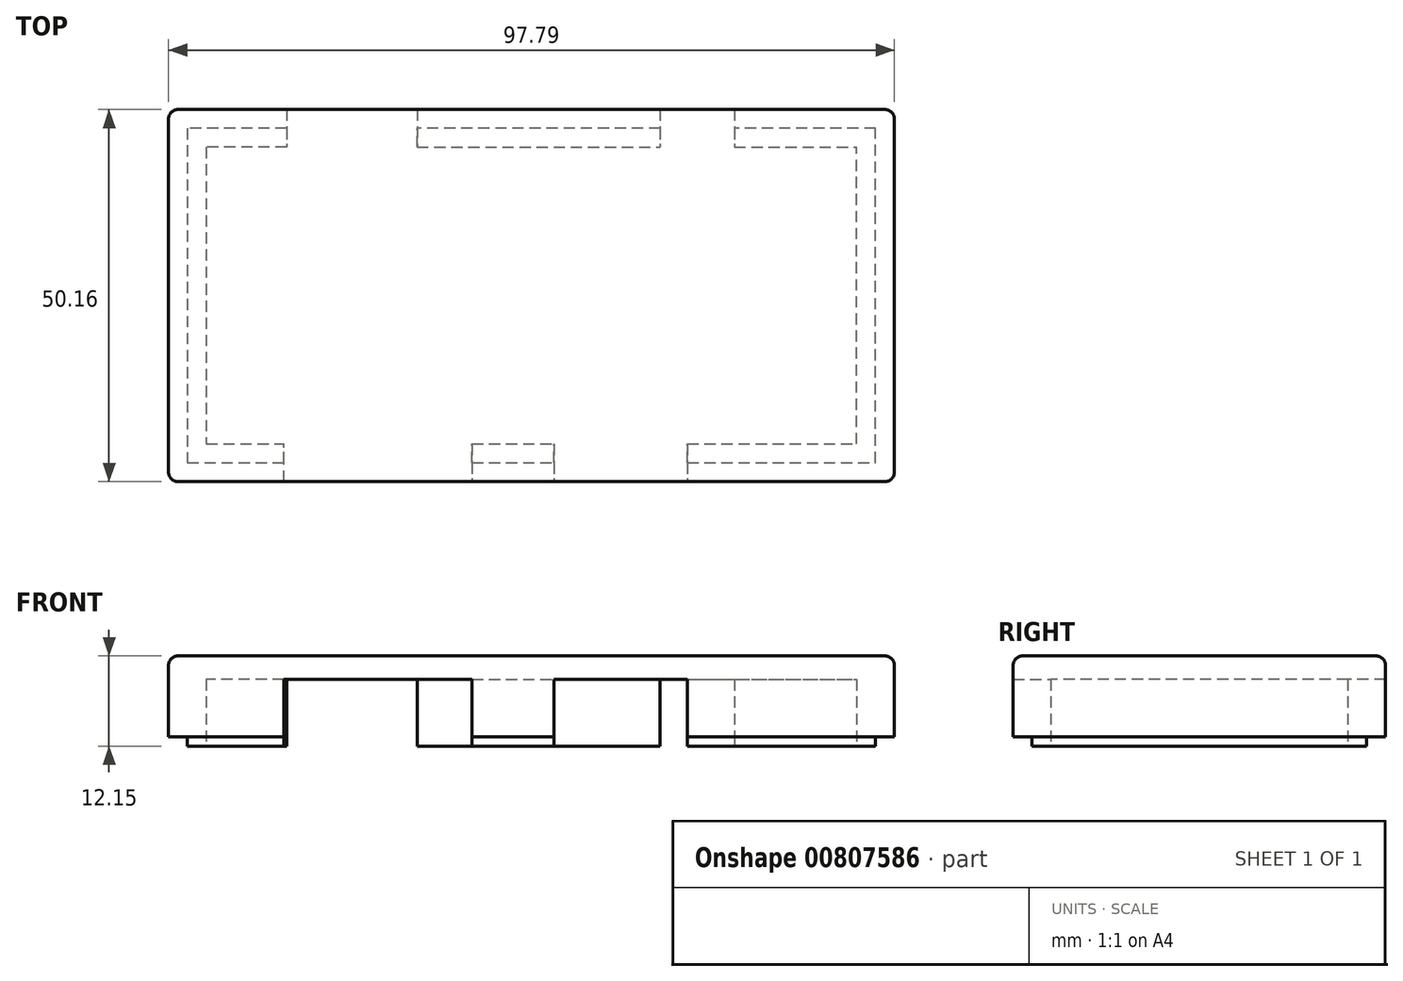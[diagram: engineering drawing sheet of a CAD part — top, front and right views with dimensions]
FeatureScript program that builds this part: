
annotation { "Feature Type Name" : "Feature", "Feature Type Description" : "" }
export const myFeature = defineFeature(function(context is Context, id is Id, definition is map)
    precondition{}
    {
        {
            var Q0;
            Q0=qCreatedBy(makeId("Top.planeOp"),FACE);
            var sketch = newSketch(context, id + "F0", { "sketchPlane" : qUnion([Q0])});
            skLineSegment(sketch, "E0.0", {"start": v(13.35, 45.09) * mm, "end": v(0, 45.09) * mm});
            skLineSegment(sketch, "E0.1", {"start": v(0, 45.09) * mm, "end": v(0, 0) * mm});
            skLineSegment(sketch, "E0.2", {"start": v(0, 0) * mm, "end": v(12.99, 0) * mm});
            skLineSegment(sketch, "E0.3", {"start": v(2.54, 2.54) * mm, "end": v(12.99, 2.54) * mm});
            skLineSegment(sketch, "E0.4", {"start": v(2.54, 42.55) * mm, "end": v(2.54, 2.54) * mm});
            skLineSegment(sketch, "E0.5", {"start": v(90.17, 42.55) * mm, "end": v(73.69, 42.55) * mm});
            skLineSegment(sketch, "E0.6", {"start": v(13.35, 45.09) * mm, "end": v(13.35, 47.63) * mm, "construction": true});
            skLineSegment(sketch, "E0.7", {"start": v(30.95, 45.09) * mm, "end": v(30.95, 47.63) * mm, "construction": true});
            skLineSegment(sketch, "E0.8", {"start": v(63.69, 45.09) * mm, "end": v(30.95, 45.09) * mm});
            skLineSegment(sketch, "E0.9", {"start": v(63.69, 45.09) * mm, "end": v(63.69, 47.63) * mm, "construction": true});
            skLineSegment(sketch, "E0.10", {"start": v(73.69, 45.09) * mm, "end": v(73.69, 47.63) * mm, "construction": true});
            skLineSegment(sketch, "E0.11", {"start": v(92.71, 45.09) * mm, "end": v(73.69, 45.09) * mm});
            skLineSegment(sketch, "E0.12", {"start": v(90.17, 2.54) * mm, "end": v(90.17, 42.55) * mm});
            skLineSegment(sketch, "E0.13", {"start": v(92.71, 0) * mm, "end": v(92.71, 45.09) * mm});
            skLineSegment(sketch, "E0.14", {"start": v(67.35, 0) * mm, "end": v(92.71, 0) * mm});
            skLineSegment(sketch, "E0.15", {"start": v(67.35, 0) * mm, "end": v(67.35, -2.54) * mm, "construction": true});
            skLineSegment(sketch, "E0.16", {"start": v(49.35, 0) * mm, "end": v(49.35, -2.54) * mm, "construction": true});
            skLineSegment(sketch, "E0.17", {"start": v(38.34, 0) * mm, "end": v(49.35, 0) * mm});
            skLineSegment(sketch, "E0.18", {"start": v(38.34, 0) * mm, "end": v(38.34, -2.54) * mm, "construction": true});
            skLineSegment(sketch, "E0.19", {"start": v(12.99, 0) * mm, "end": v(12.99, -2.54) * mm, "construction": true});
            skLineSegment(sketch, "E1", {"start": v(13.35, 45.09) * mm, "end": v(13.35, 42.55) * mm});
            skLineSegment(sketch, "E2", {"start": v(30.95, 42.55) * mm, "end": v(30.95, 45.09) * mm});
            skLineSegment(sketch, "E3", {"start": v(63.69, 45.09) * mm, "end": v(63.69, 42.55) * mm});
            skLineSegment(sketch, "E4", {"start": v(73.69, 45.09) * mm, "end": v(73.69, 42.55) * mm});
            skLineSegment(sketch, "E5.trimOffspring", {"start": v(13.35, 42.55) * mm, "end": v(2.54, 42.55) * mm});
            skLineSegment(sketch, "E6.trimOffspring", {"start": v(63.69, 42.55) * mm, "end": v(30.95, 42.55) * mm});
            skLineSegment(sketch, "E7", {"start": v(12.99, 0) * mm, "end": v(12.99, 2.54) * mm});
            skLineSegment(sketch, "E8", {"start": v(38.34, 0) * mm, "end": v(38.34, 2.54) * mm});
            skLineSegment(sketch, "E9", {"start": v(49.35, 0) * mm, "end": v(49.35, 2.54) * mm});
            skLineSegment(sketch, "E10", {"start": v(67.35, 0) * mm, "end": v(67.35, 2.54) * mm});
            skLineSegment(sketch, "E11.trimOffspring", {"start": v(38.34, 2.54) * mm, "end": v(49.35, 2.54) * mm});
            skLineSegment(sketch, "E12.trimOffspring", {"start": v(67.35, 2.54) * mm, "end": v(90.17, 2.54) * mm});
            skSolve(sketch);
        }
        {
            var Q0;
            Q0 = qSketchRegion(id + "F0", true);
            extrude(context, id + "F1", {"entities" : qUnion([Q0]), "depth" : 1.27 * mm, "offsetDistance" : 25.4 * mm});
        }
        {
            var Q0;
            Q0=makeQuery(id+"F1.opExtrude","CAP_FACE",FACE,{"disambiguationData":[OSD([sQuery(id+"F0.wireOp",EDGE,"E0.0"),sQuery(id+"F0.wireOp",EDGE,"E0.1"),sQuery(id+"F0.wireOp",EDGE,"E0.2"),sQuery(id+"F0.wireOp",EDGE,"E0.3"),sQuery(id+"F0.wireOp",EDGE,"E0.4"),sQuery(id+"F0.wireOp",EDGE,"E1"),sQuery(id+"F0.wireOp",EDGE,"E5.trimOffspring"),sQuery(id+"F0.wireOp",EDGE,"E7")])],"isStart":false});
            var sketch = newSketch(context, id + "F2", { "sketchPlane" : qUnion([Q0])});
            skPoint(sketch, "E13.0", {"position": v(2.54, 2.54) * mm});
            skPoint(sketch, "E13.1", {"position": v(90.17, 42.55) * mm});
            skLineSegment(sketch, "E14.bottom", {"start": v(2.54, 2.54) * mm, "end": v(12.99, 2.54) * mm});
            skLineSegment(sketch, "E14.top", {"start": v(2.54, 42.55) * mm, "end": v(13.35, 42.55) * mm});
            skLineSegment(sketch, "E14.left", {"start": v(2.54, 2.54) * mm, "end": v(2.54, 42.55) * mm});
            skLineSegment(sketch, "E14.right", {"start": v(90.17, 2.54) * mm, "end": v(90.17, 42.55) * mm});
            skLineSegment(sketch, "E15.0", {"start": v(-2.54, 47.63) * mm, "end": v(13.35, 47.63) * mm});
            skLineSegment(sketch, "E15.1", {"start": v(-2.54, -2.54) * mm, "end": v(-2.54, 47.63) * mm});
            skLineSegment(sketch, "E15.2", {"start": v(-2.54, -2.54) * mm, "end": v(12.99, -2.54) * mm});
            skLineSegment(sketch, "E15.3", {"start": v(95.25, -2.54) * mm, "end": v(95.25, 47.63) * mm});
            skLineSegment(sketch, "E16", {"start": v(13.35, 42.55) * mm, "end": v(13.35, 47.63) * mm});
            skLineSegment(sketch, "E17", {"start": v(30.95, 47.63) * mm, "end": v(30.95, 42.55) * mm});
            skLineSegment(sketch, "E18", {"start": v(63.69, 47.63) * mm, "end": v(63.69, 42.55) * mm});
            skLineSegment(sketch, "E19", {"start": v(73.69, 47.63) * mm, "end": v(73.69, 42.55) * mm});
            skLineSegment(sketch, "E20", {"start": v(12.99, 2.54) * mm, "end": v(12.99, -2.54) * mm});
            skLineSegment(sketch, "E21", {"start": v(38.34, 2.54) * mm, "end": v(38.34, -2.54) * mm});
            skLineSegment(sketch, "E22", {"start": v(49.35, 2.54) * mm, "end": v(49.35, -2.54) * mm});
            skLineSegment(sketch, "E23", {"start": v(67.35, 2.54) * mm, "end": v(67.35, -2.54) * mm});
            skLineSegment(sketch, "E24.trimOffspring", {"start": v(30.95, 42.55) * mm, "end": v(63.69, 42.55) * mm});
            skLineSegment(sketch, "E25.trimOffspring", {"start": v(30.95, 47.63) * mm, "end": v(63.69, 47.63) * mm});
            skLineSegment(sketch, "E26.trimOffspring", {"start": v(73.69, 47.63) * mm, "end": v(95.25, 47.63) * mm});
            skLineSegment(sketch, "E27.trimOffspring", {"start": v(73.69, 42.55) * mm, "end": v(90.17, 42.55) * mm});
            skLineSegment(sketch, "E28.trimOffspring", {"start": v(67.35, -2.54) * mm, "end": v(95.25, -2.54) * mm});
            skLineSegment(sketch, "E29.trimOffspring", {"start": v(67.35, 2.54) * mm, "end": v(90.17, 2.54) * mm});
            skLineSegment(sketch, "E30.trimOffspring", {"start": v(38.34, 2.54) * mm, "end": v(49.35, 2.54) * mm});
            skLineSegment(sketch, "E31.trimOffspring", {"start": v(38.34, -2.54) * mm, "end": v(49.35, -2.54) * mm});
            skSolve(sketch);
        }
        {
            var Q0;
            Q0 = qSketchRegion(id + "F2", true);
            extrude(context, id + "F3", {"entities" : qUnion([Q0]), "operationType" : NewBodyOperationType.ADD, "depth" : 7.7 * mm, "offsetDistance" : 25.4 * mm});
        }
        {
            var Q0;
            Q0=makeQuery(id+"F3.opExtrude","CAP_FACE",FACE,{"disambiguationData":[OSD([sQuery(id+"F2.wireOp",EDGE,"E14.bottom"),sQuery(id+"F2.wireOp",EDGE,"E14.top"),sQuery(id+"F2.wireOp",EDGE,"E14.left"),sQuery(id+"F2.wireOp",EDGE,"E15.0"),sQuery(id+"F2.wireOp",EDGE,"E15.1"),sQuery(id+"F2.wireOp",EDGE,"E15.2"),sQuery(id+"F2.wireOp",EDGE,"E16"),sQuery(id+"F2.wireOp",EDGE,"E20")])],"isStart":false});
            var sketch = newSketch(context, id + "F4", { "sketchPlane" : qUnion([Q0])});
            skPoint(sketch, "E32.0", {"position": v(95.25, 47.63) * mm});
            skPoint(sketch, "E33.0", {"position": v(-2.54, -2.54) * mm});
            skLineSegment(sketch, "E34.bottom", {"start": v(-2.54, -2.54) * mm, "end": v(95.25, -2.54) * mm});
            skLineSegment(sketch, "E34.top", {"start": v(-2.54, 47.63) * mm, "end": v(95.25, 47.63) * mm});
            skLineSegment(sketch, "E34.left", {"start": v(-2.54, -2.54) * mm, "end": v(-2.54, 47.63) * mm});
            skLineSegment(sketch, "E34.right", {"start": v(95.25, -2.54) * mm, "end": v(95.25, 47.63) * mm});
            skSolve(sketch);
        }
        {
            var Q0;
            Q0 = qSketchRegion(id + "F4", true);
            extrude(context, id + "F5", {"entities" : qUnion([Q0]), "operationType" : NewBodyOperationType.ADD, "depth" : 3.17 * mm, "offsetDistance" : 25.4 * mm});
        }
        {
            var Q0;
            Q0=makeQuery(id+"F5.boolean.opBoolean","MERGE",EDGE,{"derivedFrom":[makeQuery(id+"F3.opExtrude","SWEPT_EDGE",EDGE,{"disambiguationData":[OSD([sQuery(id+"F2.wireOp",EDGE,"E15.3"),sQuery(id+"F2.wireOp",EDGE,"E28.trimOffspring")])]}),makeQuery(id+"F5.opExtrude","SWEPT_EDGE",EDGE,{"disambiguationData":[OSD([sQuery(id+"F4.wireOp",EDGE,"E34.bottom"),sQuery(id+"F4.wireOp",EDGE,"E34.right")])]})]});
            var Q1;
            Q1=makeQuery(id+"F5.boolean.opBoolean","MERGE",EDGE,{"derivedFrom":[makeQuery(id+"F3.opExtrude","SWEPT_EDGE",EDGE,{"disambiguationData":[OSD([sQuery(id+"F2.wireOp",EDGE,"E15.1"),sQuery(id+"F2.wireOp",EDGE,"E15.2")])]}),makeQuery(id+"F5.opExtrude","SWEPT_EDGE",EDGE,{"disambiguationData":[OSD([sQuery(id+"F4.wireOp",EDGE,"E34.bottom"),sQuery(id+"F4.wireOp",EDGE,"E34.left")])]})]});
            var Q2;
            Q2=makeQuery(id+"F5.boolean.opBoolean","MERGE",EDGE,{"derivedFrom":[makeQuery(id+"F3.opExtrude","SWEPT_EDGE",EDGE,{"disambiguationData":[OSD([sQuery(id+"F2.wireOp",EDGE,"E15.3"),sQuery(id+"F2.wireOp",EDGE,"E26.trimOffspring")])]}),makeQuery(id+"F5.opExtrude","SWEPT_EDGE",EDGE,{"disambiguationData":[OSD([sQuery(id+"F4.wireOp",EDGE,"E34.top"),sQuery(id+"F4.wireOp",EDGE,"E34.right")])]})]});
            var Q3;
            Q3=makeQuery(id+"F5.boolean.opBoolean","MERGE",EDGE,{"derivedFrom":[makeQuery(id+"F3.opExtrude","SWEPT_EDGE",EDGE,{"disambiguationData":[OSD([sQuery(id+"F2.wireOp",EDGE,"E15.0"),sQuery(id+"F2.wireOp",EDGE,"E15.1")])]}),makeQuery(id+"F5.opExtrude","SWEPT_EDGE",EDGE,{"disambiguationData":[OSD([sQuery(id+"F4.wireOp",EDGE,"E34.top"),sQuery(id+"F4.wireOp",EDGE,"E34.left")])]})]});
            var Q4;
            Q4=makeQuery(id+"F5.opExtrude","CAP_FACE",FACE,{"disambiguationData":[OSD([sQuery(id+"F4.wireOp",EDGE,"E34.bottom"),sQuery(id+"F4.wireOp",EDGE,"E34.top"),sQuery(id+"F4.wireOp",EDGE,"E34.left"),sQuery(id+"F4.wireOp",EDGE,"E34.right")])],"isStart":false});
            fillet(context, id + "F6", {"entities" : qUnion([Q0, Q1, Q2, Q3, Q4]), "radius" : 1.27 * mm, "tangentPropagation" : true, "allowEdgeOverflow" : false});
        }
    });
